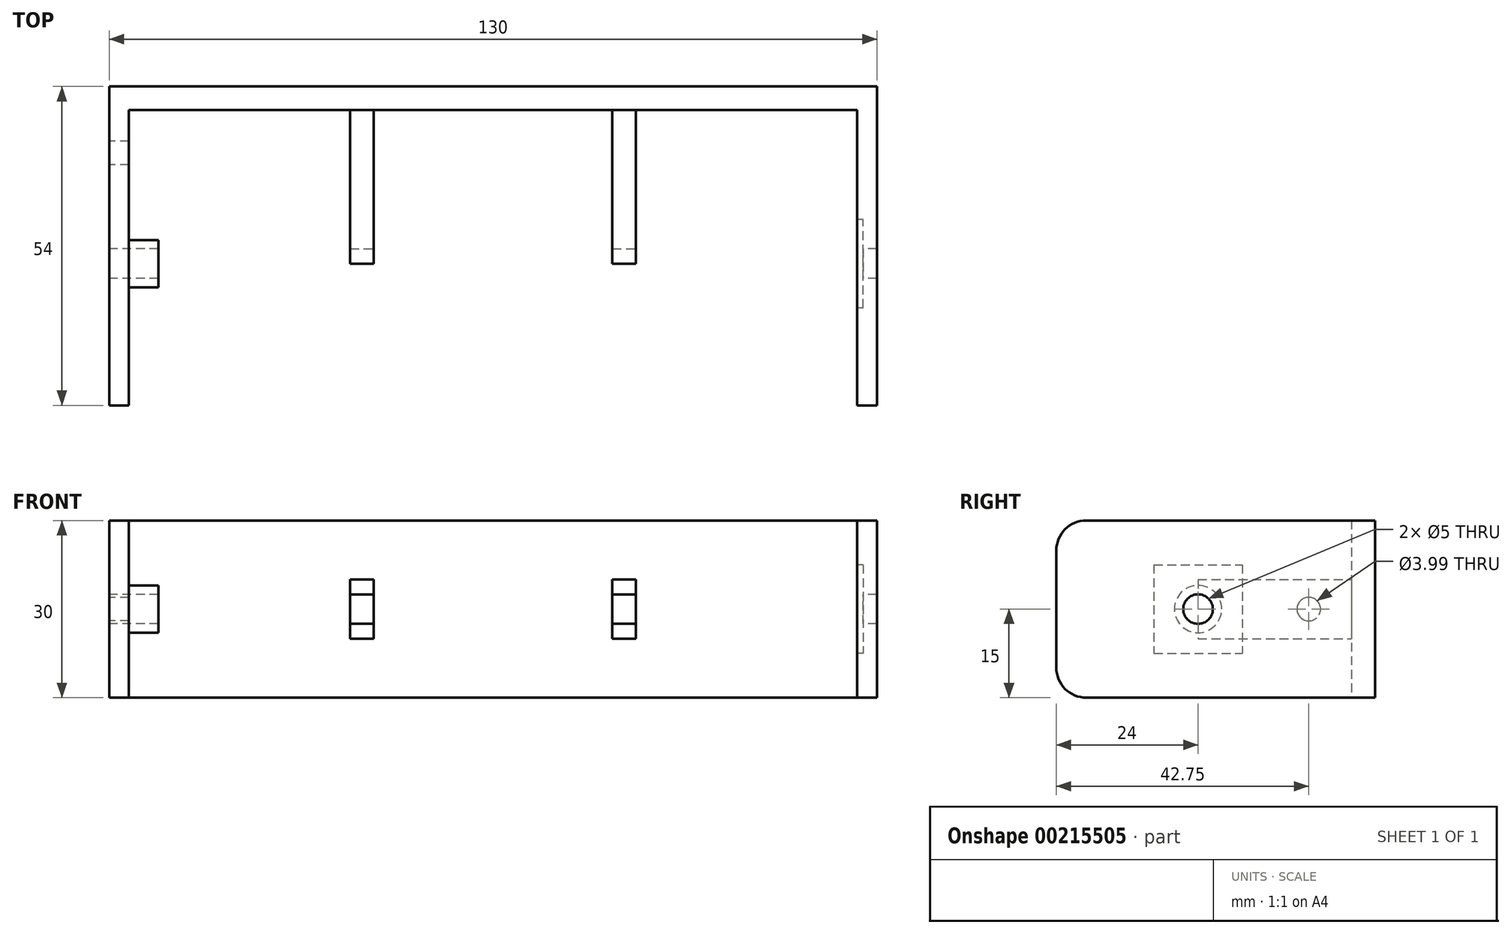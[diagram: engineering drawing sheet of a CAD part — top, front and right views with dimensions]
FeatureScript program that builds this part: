
annotation { "Feature Type Name" : "Feature", "Feature Type Description" : "" }
export const myFeature = defineFeature(function(context is Context, id is Id, definition is map)
    precondition{}
    {
        {
            var Q0;
            Q0=qCreatedBy(makeId("Front.planeOp"),FACE);
            var sketch = newSketch(context, id + "F0", { "sketchPlane" : qUnion([Q0])});
            skLineSegment(sketch, "E0.bottom", {"start": v(-65, 15) * mm, "end": v(65, 15) * mm});
            skLineSegment(sketch, "E0.top", {"start": v(-65, -15) * mm, "end": v(65, -15) * mm});
            skLineSegment(sketch, "E0.left", {"start": v(-65, 15) * mm, "end": v(-65, -15) * mm});
            skLineSegment(sketch, "E0.right", {"start": v(65, 15) * mm, "end": v(65, -15) * mm});
            skPoint(sketch, "E0.middle", {"position": v(0, 0) * mm});
            skSolve(sketch);
        }
        {
            var Q0;
            Q0 = qSketchRegion(id + "F0", true);
            var Q1;
            Q1 = qSketchRegion(id + "F2", true);
            extrude(context, id + "F1", {"entities" : qUnion([Q0, Q1]), "depth" : 4 * mm});
        }
        {
            var Q0;
            Q0=makeQuery(id+"F1.opExtrude","CAP_FACE",FACE,{"disambiguationData":[OSD([sQuery(id+"F0.wireOp",EDGE,"E0.bottom"),sQuery(id+"F0.wireOp",EDGE,"E0.top"),sQuery(id+"F0.wireOp",EDGE,"E0.left"),sQuery(id+"F0.wireOp",EDGE,"E0.right")])],"isStart":false});
            var sketch = newSketch(context, id + "F2", { "sketchPlane" : qUnion([Q0])});
            skLineSegment(sketch, "E1.bottom", {"start": v(-65, 15) * mm, "end": v(-61.67, 15) * mm});
            skLineSegment(sketch, "E1.top", {"start": v(-65, -15) * mm, "end": v(-61.67, -15) * mm});
            skLineSegment(sketch, "E1.left", {"start": v(-65, 15) * mm, "end": v(-65, -15) * mm});
            skLineSegment(sketch, "E1.right", {"start": v(-61.67, 15) * mm, "end": v(-61.67, -15) * mm});
            skLineSegment(sketch, "E2.bottom", {"start": v(65, 15) * mm, "end": v(61.67, 15) * mm});
            skLineSegment(sketch, "E2.top", {"start": v(65, -15) * mm, "end": v(61.67, -15) * mm});
            skLineSegment(sketch, "E2.left", {"start": v(65, 15) * mm, "end": v(65, -15) * mm});
            skLineSegment(sketch, "E2.right", {"start": v(61.67, 15) * mm, "end": v(61.67, -15) * mm});
            skSolve(sketch);
        }
        {
            var Q0;
            Q0=makeQuery(id+"F2.imprint","IMPRINT",FACE,{"disambiguationData":[TD([[makeQuery(id+"F2.imprint","IMPRINT",EDGE,{"derivedFrom":sQuery(id+"F2.wireOp",EDGE,"E1.bottom")}),-1.0]])]});
            var Q1;
            Q1=makeQuery(id+"F2.imprint","IMPRINT",FACE,{"disambiguationData":[TD([[makeQuery(id+"F2.imprint","IMPRINT",EDGE,{"derivedFrom":sQuery(id+"F2.wireOp",EDGE,"E2.bottom")}),-1.0]])]});
            extrude(context, id + "F3", {"entities" : qUnion([Q0, Q1]), "operationType" : NewBodyOperationType.ADD, "depth" : 50 * mm});
        }
        {
            var Q0;
            Q0=makeQuery(id+"F3.opExtrude","CAP_EDGE",EDGE,{"disambiguationData":[OSD([sQuery(id+"F2.wireOp",EDGE,"E2.bottom")])],"isStart":false});
            var Q1;
            Q1=makeQuery(id+"F3.opExtrude","CAP_EDGE",EDGE,{"disambiguationData":[OSD([sQuery(id+"F2.wireOp",EDGE,"E2.top")])],"isStart":false});
            var Q2;
            Q2=makeQuery(id+"F3.opExtrude","CAP_EDGE",EDGE,{"disambiguationData":[OSD([sQuery(id+"F2.wireOp",EDGE,"E1.top")])],"isStart":false});
            var Q3;
            Q3=makeQuery(id+"F3.opExtrude","CAP_EDGE",EDGE,{"disambiguationData":[OSD([sQuery(id+"F2.wireOp",EDGE,"E1.bottom")])],"isStart":false});
            fillet(context, id + "F4", {"entities" : qUnion([Q0, Q1, Q2, Q3]), "radius" : 5.08 * mm, "tangentPropagation" : true, "allowEdgeOverflow" : false});
        }
        {
            var Q0;
            Q0=makeQuery(id+"F3.boolean.opBoolean","MERGE",FACE,{"derivedFrom":[makeQuery(id+"F1.opExtrude","SWEPT_FACE",FACE,{"disambiguationData":[OSD([sQuery(id+"F0.wireOp",EDGE,"E0.left")])]}),makeQuery(id+"F3.opExtrude","SWEPT_FACE",FACE,{"disambiguationData":[OSD([sQuery(id+"F2.wireOp",EDGE,"E1.left")])]})]});
            var sketch = newSketch(context, id + "F5", { "sketchPlane" : qUnion([Q0])});
            skLineSegment(sketch, "E3", {"start": v(-38.98, 0) * mm, "end": v(87.42, 0) * mm, "construction": true});
            skPoint(sketch, "E3.startSnap0", {"position": v(0, 0) * mm});
            skCircle(sketch, "E4", {"center": v(30, 0) * mm, "radius": 2.5 * mm});
            skSolve(sketch);
        }
        {
            var Q0;
            Q0=makeQuery(id+"F5.imprint","IMPRINT",FACE,{"disambiguationData":[TD([[makeQuery(id+"F5.imprint","IMPRINT",EDGE,{"derivedFrom":sQuery(id+"F5.wireOp",EDGE,"E4")}),1.0]])]});
            var Q1;
            Q1=sQuery(id+"F5.wireOp",EDGE,"E4");
            extrude(context, id + "F6", {"entities" : qUnion([Q0]), "operationType" : NewBodyOperationType.REMOVE, "surfaceEntities" : qUnion([Q1]), "oppositeDirection" : true, "depth" : 137.16 * mm});
        }
        {
            var Q0;
            Q0=makeQuery(id+"F3.opExtrude","SWEPT_FACE",FACE,{"disambiguationData":[OSD([sQuery(id+"F2.wireOp",EDGE,"E1.right")])]});
            var sketch = newSketch(context, id + "F7", { "sketchPlane" : qUnion([Q0])});
            skCircle(sketch, "E5", {"center": v(-30, 0) * mm, "radius": 4 * mm});
            skCircle(sketch, "E6.0", {"center": v(-30, 0) * mm, "radius": 2.5 * mm});
            skSolve(sketch);
        }
        {
            var Q0;
            Q0 = qSketchRegion(id + "F7", true);
            extrude(context, id + "F8", {"entities" : qUnion([Q0]), "operationType" : NewBodyOperationType.ADD, "depth" : 5 * mm});
        }
        {
            var Q0;
            Q0=makeQuery(id+"F3.opExtrude","SWEPT_FACE",FACE,{"disambiguationData":[OSD([sQuery(id+"F2.wireOp",EDGE,"E2.right")])]});
            var sketch = newSketch(context, id + "F9", { "sketchPlane" : qUnion([Q0])});
            skCircle(sketch, "E7.0", {"center": v(30, 0) * mm, "radius": 2.5 * mm});
            skLineSegment(sketch, "E8.bottom", {"start": v(37.5, 7.5) * mm, "end": v(22.5, 7.5) * mm});
            skLineSegment(sketch, "E8.top", {"start": v(37.5, -7.5) * mm, "end": v(22.5, -7.5) * mm});
            skLineSegment(sketch, "E8.left", {"start": v(37.5, 7.5) * mm, "end": v(37.5, -7.5) * mm});
            skLineSegment(sketch, "E8.right", {"start": v(22.5, 7.5) * mm, "end": v(22.5, -7.5) * mm});
            skSolve(sketch);
        }
        {
            var Q0;
            Q0 = qSketchRegion(id + "F9", true);
            extrude(context, id + "F10", {"entities" : qUnion([Q0]), "operationType" : NewBodyOperationType.REMOVE, "oppositeDirection" : true, "depth" : 1 * mm});
        }
        {
            var Q0;
            Q0=makeQuery(id+"F1.opExtrude","CAP_FACE",FACE,{"disambiguationData":[OSD([sQuery(id+"F0.wireOp",EDGE,"E0.bottom"),sQuery(id+"F0.wireOp",EDGE,"E0.top"),sQuery(id+"F0.wireOp",EDGE,"E0.left"),sQuery(id+"F0.wireOp",EDGE,"E0.right")])],"isStart":false});
            var sketch = newSketch(context, id + "F11", { "sketchPlane" : qUnion([Q0])});
            skLineSegment(sketch, "E9", {"start": v(-112.36, 0) * mm, "end": v(85.43, 0) * mm, "construction": true});
            skLineSegment(sketch, "E10", {"start": v(0, 64.6) * mm, "end": v(0, -53.71) * mm, "construction": true});
            skPoint(sketch, "E10.endSnap0", {"position": v(0, -15) * mm});
            skLineSegment(sketch, "E11.bottom", {"start": v(-20.2, 5) * mm, "end": v(-24.2, 5) * mm});
            skLineSegment(sketch, "E11.top", {"start": v(-20.2, -5) * mm, "end": v(-24.2, -5) * mm});
            skLineSegment(sketch, "E11.left", {"start": v(-20.2, 5) * mm, "end": v(-20.2, -5) * mm});
            skLineSegment(sketch, "E11.right", {"start": v(-24.2, 5) * mm, "end": v(-24.2, -5) * mm});
            skPoint(sketch, "E11.middle", {"position": v(-22.2, 0) * mm});
            skLineSegment(sketch, "E12.MirrorCS", {"start": v(20.2, 5) * mm, "end": v(20.2, -5) * mm});
            skLineSegment(sketch, "E13.MirrorCS", {"start": v(20.2, 5) * mm, "end": v(24.2, 5) * mm});
            skLineSegment(sketch, "E14.MirrorCS", {"start": v(20.2, -5) * mm, "end": v(24.2, -5) * mm});
            skLineSegment(sketch, "E15.MirrorCS", {"start": v(24.2, 5) * mm, "end": v(24.2, -5) * mm});
            skSolve(sketch);
        }
        {
            var Q0;
            Q0=makeQuery(id+"F11.imprint","IMPRINT",FACE,{"disambiguationData":[TD([[makeQuery(id+"F11.imprint","IMPRINT",EDGE,{"derivedFrom":sQuery(id+"F11.wireOp",EDGE,"E11.bottom")}),1.0]])]});
            var Q1;
            Q1=makeQuery(id+"F11.imprint","IMPRINT",FACE,{"disambiguationData":[TD([[makeQuery(id+"F11.imprint","IMPRINT",EDGE,{"derivedFrom":sQuery(id+"F11.wireOp",EDGE,"E12.MirrorCS")}),1.0]])]});
            extrude(context, id + "F12", {"entities" : qUnion([Q0, Q1]), "operationType" : NewBodyOperationType.ADD, "depth" : 26 * mm});
        }
        {
            var Q0;
            Q0=makeQuery(id+"F12.opExtrude","SWEPT_FACE",FACE,{"disambiguationData":[OSD([sQuery(id+"F11.wireOp",EDGE,"E11.left")])]});
            var sketch = newSketch(context, id + "F13", { "sketchPlane" : qUnion([Q0])});
            skCircle(sketch, "E16.0", {"center": v(-30, 0) * mm, "radius": 2.5 * mm});
            skSolve(sketch);
        }
        {
            var Q0;
            {var subQ0=sQuery(id+"F13.wireOp",EDGE,"E16.0");var subQ1=makeQuery(id+"F12.opExtrude","CAP_EDGE",EDGE,{"disambiguationData":[OSD([sQuery(id+"F11.wireOp",EDGE,"E11.left")])],"isStart":false});var subQ2=makeQuery(id+"F13.imprint","INTERSECT",VERTEX,{"disambiguationData":[OD(0.0)],"derivedFrom":[subQ1,subQ0]});Q0=makeQuery(id+"F13.imprint","IMPRINT",FACE,{"disambiguationData":[TD([[makeQuery(id+"F13.imprint","IMPRINT",EDGE,{"disambiguationData":[TD([[subQ2,1.0]])],"derivedFrom":subQ0}),1.0]])]});}
            var Q1;
            Q1=sQuery(id+"F13.wireOp",EDGE,"E16.0");
            extrude(context, id + "F14", {"entities" : qUnion([Q0]), "operationType" : NewBodyOperationType.REMOVE, "surfaceEntities" : qUnion([Q1]), "oppositeDirection" : true, "depth" : 14.22 * mm});
        }
        {
            var Q0;
            Q0=makeQuery(id+"F12.opExtrude","SWEPT_FACE",FACE,{"disambiguationData":[OSD([sQuery(id+"F11.wireOp",EDGE,"E15.MirrorCS")])]});
            var sketch = newSketch(context, id + "F15", { "sketchPlane" : qUnion([Q0])});
            skArc(sketch, "E17.0", {"start": v(-30, -2.5) * mm, "mid": v(-27.5, 0) * mm, "end": v(-30, 2.5) * mm});
            skSolve(sketch);
        }
        {
            var Q0;
            {var subQ0=sQuery(id+"F15.wireOp",EDGE,"E17.0");Q0=makeQuery(id+"F15.imprint","IMPRINT",FACE,{"disambiguationData":[TD([[makeQuery(id+"F15.imprint","IMPRINT",EDGE,{"derivedFrom":subQ0}),1.0]])]});}
            extrude(context, id + "F16", {"entities" : qUnion([Q0]), "operationType" : NewBodyOperationType.REMOVE, "oppositeDirection" : true, "depth" : 6.1 * mm});
        }
        {
            var Q0;
            Q0=makeQuery(id+"F3.boolean.opBoolean","MERGE",FACE,{"derivedFrom":[makeQuery(id+"F1.opExtrude","SWEPT_FACE",FACE,{"disambiguationData":[OSD([sQuery(id+"F0.wireOp",EDGE,"E0.left")])]}),makeQuery(id+"F3.opExtrude","SWEPT_FACE",FACE,{"disambiguationData":[OSD([sQuery(id+"F2.wireOp",EDGE,"E1.left")])]})]});
            var sketch = newSketch(context, id + "F17", { "sketchPlane" : qUnion([Q0])});
            skLineSegment(sketch, "E18", {"start": v(-68.61, 0) * mm, "end": v(175.5, 0) * mm, "construction": true});
            skPoint(sketch, "E18.endSnap0", {"position": v(54, 0) * mm});
            skCircle(sketch, "E19", {"center": v(11.25, 0) * mm, "radius": 2 * mm});
            skCircle(sketch, "E20.0", {"center": v(30, 0) * mm, "radius": 2.5 * mm});
            skLineSegment(sketch, "E21.0", {"start": v(0, 15) * mm, "end": v(0, -15) * mm, "construction": true});
            skPoint(sketch, "E22", {"position": v(0, 0) * mm});
            skSolve(sketch);
        }
        {
            var Q0;
            Q0=makeQuery(id+"F17.imprint","IMPRINT",FACE,{"disambiguationData":[TD([[makeQuery(id+"F17.imprint","IMPRINT",EDGE,{"derivedFrom":sQuery(id+"F17.wireOp",EDGE,"E19")}),1.0]])]});
            var Q1;
            Q1=sQuery(id+"F17.wireOp",EDGE,"E19");
            extrude(context, id + "F18", {"entities" : qUnion([Q0]), "operationType" : NewBodyOperationType.REMOVE, "surfaceEntities" : qUnion([Q1]), "oppositeDirection" : true, "depth" : 25.4 * mm});
        }
    });
